# Revit family: LSTG 1x4
name_source: partatom
category: Lighting Fixtures
units: mm (PartAtom-declared; Revit-internal decimal feet)

## family parameters
Always vertical = Yes
Cut with Voids When Loaded = No
Host = Ceiling
Light Source = Yes
OmniClass Number = 23.80.70.11.14.17
OmniClass Title = Direct/Indirect
Part Type = Normal
Room Calculation Point = No
Round Connector Dimension = Use Diameter
Shared = No

## types (1)
- LSTG1x4-LED840K040LUNV
    Apparent Load = 34 VA
    Assembly Code = D5020200
    Color Filter = 16777215
    Description = LED Surface Type G
    Dimming Lamp Color Temperature Shift = <None>
    Emit Shape Visible in Rendering = No
    Emit from Rectangle Length = 3' - 11 3/4"
    Emit from Rectangle Width = 0' - 11 3/4"
    Housing Finish = Metal - Viscor - White
    Lamp = LED
    Lamp Wattage = 34 VA
    Length = 3' - 11 3/4"
    Lens Finish = Acrylic - Viscor - Impact Resistant Frosted White
    Manufacturer = VISIONEERING by VISCOR
    Model = LSTG
    Photometric Web File = LSTG1x4-LED840K040LUNV.IES
    Reflector Width = 0' - 5 7/8"
    Tilt Angle = 90.00°
    URL = https://www.viscor.com
    Voltage = 120 V
    Width = 0' - 11 3/4"

## geometry (parser evidence)
native form markers: Sweep x3
no freeform markers — native parametric forms only
